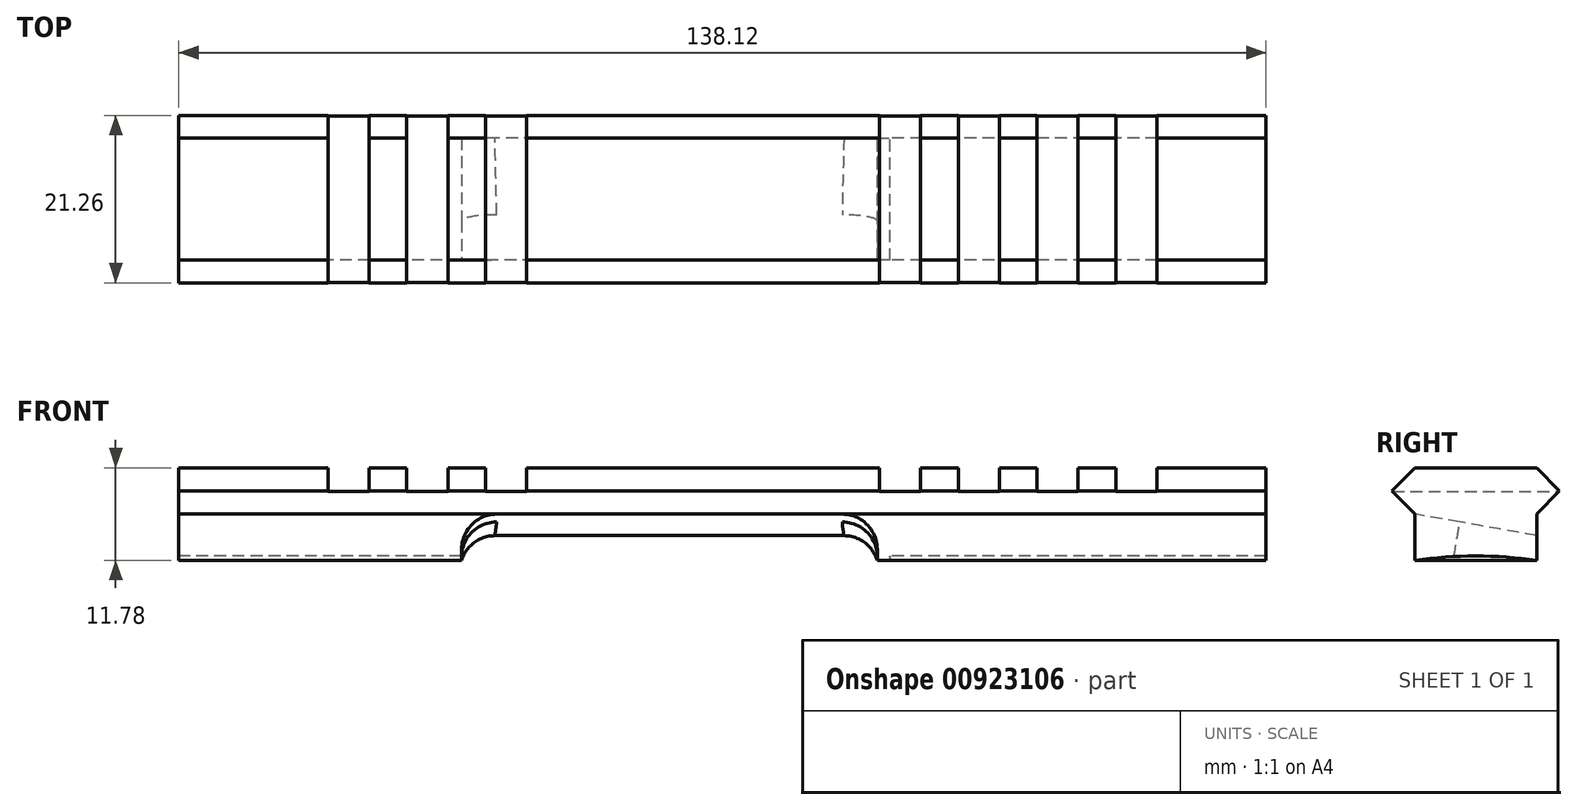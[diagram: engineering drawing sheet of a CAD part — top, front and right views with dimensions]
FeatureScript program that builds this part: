
annotation { "Feature Type Name" : "Feature", "Feature Type Description" : "" }
export const myFeature = defineFeature(function(context is Context, id is Id, definition is map)
    precondition{}
    {
        {
            var Q0;
            Q0=qCreatedBy(makeId("Right.planeOp"),FACE);
            var sketch = newSketch(context, id + "F0", { "sketchPlane" : qUnion([Q0])});
            skArc(sketch, "E0", {"start": v(15.26, -7.75) * mm, "mid": v(15.69, -3.88) * mm, "end": v(15.83, 0) * mm});
            skPoint(sketch, "E1.start.orphan", {"position": v(0, -7.82) * mm});
            skLineSegment(sketch, "E2.bottom", {"start": v(15.26, -7.75) * mm, "end": v(21.15, -7.75) * mm});
            skLineSegment(sketch, "E2.right", {"start": v(27.04, -7.75) * mm, "end": v(27.04, 0) * mm});
            skLineSegment(sketch, "E3", {"start": v(27.04, -7.75) * mm, "end": v(24.1, -10.63) * mm});
            skLineSegment(sketch, "E4", {"start": v(21.15, -7.75) * mm, "end": v(24.1, -10.63) * mm});
            skPoint(sketch, "E5.right.start.orphan", {"position": v(27.04, -7.75) * mm});
            skPoint(sketch, "E5.left.end.orphan", {"position": v(21.15, -10.63) * mm});
            skLineSegment(sketch, "E6", {"start": v(27.04, 0) * mm, "end": v(15.83, 0) * mm});
            skSolve(sketch);
        }
        {
            var Q0;
            Q0=makeQuery(id+"F0.imprint","IMPRINT",FACE,{"disambiguationData":[TD([[makeQuery(id+"F0.imprint","IMPRINT",EDGE,{"derivedFrom":sQuery(id+"F0.wireOp",EDGE,"E0")}),-1.0]])]});
            extrude(context, id + "F1", {"entities" : qUnion([Q0]), "depth" : 138.11 * mm, "offsetDistance" : 25.4 * mm, "symmetric" : true});
        }
        {
            var Q0;
            Q0=makeQuery(id+"F1.opExtrude","SWEPT_BODY",BODY,{"disambiguationData":[OSD([sQuery(id+"F0.wireOp",EDGE,"E0"),sQuery(id+"F0.wireOp",EDGE,"E2.bottom"),sQuery(id+"F0.wireOp",EDGE,"E2.right"),sQuery(id+"F0.wireOp",EDGE,"E3"),sQuery(id+"F0.wireOp",EDGE,"E4"),sQuery(id+"F0.wireOp",EDGE,"E6")])]});
            var Q1;
            Q1=qCreatedBy(makeId("Top.planeOp"),FACE);
            mirror(context, id + "F2", {"operationType" : NewBodyOperationType.ADD, "entities" : qUnion([Q0]), "mirrorPlane" : qUnion([Q1])});
        }
        {
            var Q0;
            Q0=qCreatedBy(makeId("Top.planeOp"),FACE);
            var sketch = newSketch(context, id + "F3", { "sketchPlane" : qUnion([Q0])});
            skLineSegment(sketch, "E7", {"start": v(0, 0) * mm, "end": v(78.36, 0) * mm});
            skSolve(sketch);
        }
        {
            var Q0;
            Q0=makeQuery(id+"F1.opExtrude","SWEPT_BODY",BODY,{"disambiguationData":[OSD([sQuery(id+"F0.wireOp",EDGE,"E0"),sQuery(id+"F0.wireOp",EDGE,"E2.bottom"),sQuery(id+"F0.wireOp",EDGE,"E2.right"),sQuery(id+"F0.wireOp",EDGE,"E3"),sQuery(id+"F0.wireOp",EDGE,"E4"),sQuery(id+"F0.wireOp",EDGE,"E6")])]});
            var Q1;
            Q1=sQuery(id+"F3.wireOp",VERTEX,"E7.start");
            var Q2;
            Q2=sQuery(id+"F3.wireOp",EDGE,"E7");
            transform(context, id + "F4", {"entities" : qUnion([Q0]), "transformType" : TransformType.ROTATION, "transformAxis" : qUnion([Q2]), "angle" : 90 * degree, "makeCopy" : false});
        }
        {
            var Q0;
            Q0=qCreatedBy(makeId("Front.planeOp"),FACE);
            var sketch = newSketch(context, id + "F5", { "sketchPlane" : qUnion([Q0])});
            skLineSegment(sketch, "E8.bottom", {"start": v(-50.1, 24.04) * mm, "end": v(-44.88, 24.04) * mm});
            skLineSegment(sketch, "E8.top", {"start": v(-50.1, 31.17) * mm, "end": v(-44.88, 31.17) * mm});
            skLineSegment(sketch, "E8.left", {"start": v(-50.1, 24.04) * mm, "end": v(-50.1, 31.17) * mm});
            skLineSegment(sketch, "E8.right", {"start": v(-44.88, 24.04) * mm, "end": v(-44.88, 31.17) * mm});
            skLineSegment(sketch, "E9.2.0.0", {"start": v(155.78, 24.04) * mm, "end": v(155.78, 31.17) * mm});
            skLineSegment(sketch, "E9.3.0.0", {"start": v(256.11, 24.04) * mm, "end": v(256.11, 31.17) * mm});
            skLineSegment(sketch, "E9.4.0.0", {"start": v(356.44, 24.04) * mm, "end": v(356.44, 31.17) * mm});
            skLineSegment(sketch, "E9.5.0.0", {"start": v(456.77, 24.04) * mm, "end": v(456.77, 31.17) * mm});
            skLineSegment(sketch, "E9.6.0.0", {"start": v(557.1, 24.04) * mm, "end": v(557.1, 31.17) * mm});
            skLineSegment(sketch, "E9.7.0.0", {"start": v(657.43, 24.04) * mm, "end": v(657.43, 31.17) * mm});
            skLineSegment(sketch, "E9.8.0.0", {"start": v(757.76, 24.04) * mm, "end": v(757.76, 31.17) * mm});
            skLineSegment(sketch, "E9.9.0.0", {"start": v(858.1, 24.04) * mm, "end": v(858.1, 31.17) * mm});
            skLineSegment(sketch, "E10.1.0.0", {"start": v(-40.1, 31.17) * mm, "end": v(-34.87, 31.17) * mm});
            skLineSegment(sketch, "E10.1.0.1", {"start": v(-40.1, 24.04) * mm, "end": v(-40.1, 31.17) * mm});
            skLineSegment(sketch, "E10.1.0.2", {"start": v(-40.1, 24.04) * mm, "end": v(-34.87, 24.04) * mm});
            skLineSegment(sketch, "E10.1.0.3", {"start": v(-34.87, 24.04) * mm, "end": v(-34.87, 31.17) * mm});
            skLineSegment(sketch, "E10.2.0.0", {"start": v(-30.1, 31.17) * mm, "end": v(-24.86, 31.17) * mm});
            skLineSegment(sketch, "E10.2.0.1", {"start": v(-30.1, 24.04) * mm, "end": v(-30.1, 31.17) * mm});
            skLineSegment(sketch, "E10.2.0.2", {"start": v(-30.1, 24.04) * mm, "end": v(-24.86, 24.04) * mm});
            skLineSegment(sketch, "E10.2.0.3", {"start": v(-24.86, 24.04) * mm, "end": v(-24.86, 31.17) * mm});
            skLineSegment(sketch, "E10.direction1", {"start": v(-50.1, 31.17) * mm, "end": v(-40.1, 31.17) * mm, "construction": true});
            skLineSegment(sketch, "E11.0.7.0", {"start": v(19.95, 31.17) * mm, "end": v(25.17, 31.17) * mm});
            skLineSegment(sketch, "E11.3.7.0", {"start": v(19.95, 24.04) * mm, "end": v(19.95, 31.17) * mm});
            skLineSegment(sketch, "E11.6.7.0", {"start": v(19.95, 24.04) * mm, "end": v(25.17, 24.04) * mm});
            skLineSegment(sketch, "E11.9.7.0", {"start": v(25.17, 24.04) * mm, "end": v(25.17, 31.17) * mm});
            skLineSegment(sketch, "E11.0.8.0", {"start": v(29.95, 31.17) * mm, "end": v(35.18, 31.17) * mm});
            skLineSegment(sketch, "E11.3.8.0", {"start": v(29.95, 24.04) * mm, "end": v(29.95, 31.17) * mm});
            skLineSegment(sketch, "E11.6.8.0", {"start": v(29.95, 24.04) * mm, "end": v(35.18, 24.04) * mm});
            skLineSegment(sketch, "E11.9.8.0", {"start": v(35.18, 24.04) * mm, "end": v(35.18, 31.17) * mm});
            skLineSegment(sketch, "E11.0.9.0", {"start": v(39.96, 31.17) * mm, "end": v(45.19, 31.17) * mm});
            skLineSegment(sketch, "E11.3.9.0", {"start": v(39.96, 24.04) * mm, "end": v(39.96, 31.17) * mm});
            skLineSegment(sketch, "E11.6.9.0", {"start": v(39.96, 24.04) * mm, "end": v(45.19, 24.04) * mm});
            skLineSegment(sketch, "E11.9.9.0", {"start": v(45.19, 24.04) * mm, "end": v(45.19, 31.17) * mm});
            skLineSegment(sketch, "E12.0.10.0", {"start": v(49.97, 31.17) * mm, "end": v(55.2, 31.17) * mm});
            skLineSegment(sketch, "E12.3.10.0", {"start": v(49.97, 24.04) * mm, "end": v(49.97, 31.17) * mm});
            skLineSegment(sketch, "E12.6.10.0", {"start": v(49.97, 24.04) * mm, "end": v(55.2, 24.04) * mm});
            skLineSegment(sketch, "E12.9.10.0", {"start": v(55.2, 24.04) * mm, "end": v(55.2, 31.17) * mm});
            skSolve(sketch);
        }
        {
            var Q0;
            Q0=makeQuery(id+"F5.imprint","IMPRINT",FACE,{"disambiguationData":[TD([[makeQuery(id+"F5.imprint","IMPRINT",EDGE,{"derivedFrom":sQuery(id+"F5.wireOp",EDGE,"E8.bottom")}),1.0]])]});
            var Q1;
            Q1=makeQuery(id+"F5.imprint","IMPRINT",FACE,{"disambiguationData":[TD([[makeQuery(id+"F5.imprint","IMPRINT",EDGE,{"derivedFrom":sQuery(id+"F5.wireOp",EDGE,"E10.1.0.0")}),-1.0]])]});
            var Q2;
            Q2=makeQuery(id+"F5.imprint","IMPRINT",FACE,{"disambiguationData":[TD([[makeQuery(id+"F5.imprint","IMPRINT",EDGE,{"derivedFrom":sQuery(id+"F5.wireOp",EDGE,"E10.2.0.0")}),-1.0]])]});
            var Q3;
            Q3=makeQuery(id+"F5.imprint","IMPRINT",FACE,{"disambiguationData":[TD([[makeQuery(id+"F5.imprint","IMPRINT",EDGE,{"derivedFrom":sQuery(id+"F5.wireOp",EDGE,"E11.0.3.0")}),-1.0]])]});
            var Q4;
            Q4=makeQuery(id+"F5.imprint","IMPRINT",FACE,{"disambiguationData":[TD([[makeQuery(id+"F5.imprint","IMPRINT",EDGE,{"derivedFrom":sQuery(id+"F5.wireOp",EDGE,"E11.0.4.0")}),-1.0]])]});
            var Q5;
            Q5=makeQuery(id+"F5.imprint","IMPRINT",FACE,{"disambiguationData":[TD([[makeQuery(id+"F5.imprint","IMPRINT",EDGE,{"derivedFrom":sQuery(id+"F5.wireOp",EDGE,"E11.0.5.0")}),-1.0]])]});
            var Q6;
            Q6=makeQuery(id+"F5.imprint","IMPRINT",FACE,{"disambiguationData":[TD([[makeQuery(id+"F5.imprint","IMPRINT",EDGE,{"derivedFrom":sQuery(id+"F5.wireOp",EDGE,"E11.0.6.0")}),-1.0]])]});
            var Q7;
            Q7=makeQuery(id+"F5.imprint","IMPRINT",FACE,{"disambiguationData":[TD([[makeQuery(id+"F5.imprint","IMPRINT",EDGE,{"derivedFrom":sQuery(id+"F5.wireOp",EDGE,"E11.0.7.0")}),-1.0]])]});
            var Q8;
            Q8=makeQuery(id+"F5.imprint","IMPRINT",FACE,{"disambiguationData":[TD([[makeQuery(id+"F5.imprint","IMPRINT",EDGE,{"derivedFrom":sQuery(id+"F5.wireOp",EDGE,"E11.0.8.0")}),-1.0]])]});
            var Q9;
            Q9=makeQuery(id+"F5.imprint","IMPRINT",FACE,{"disambiguationData":[TD([[makeQuery(id+"F5.imprint","IMPRINT",EDGE,{"derivedFrom":sQuery(id+"F5.wireOp",EDGE,"E11.0.9.0")}),-1.0]])]});
            var Q10;
            Q10=makeQuery(id+"F5.imprint","IMPRINT",FACE,{"disambiguationData":[TD([[makeQuery(id+"F5.imprint","IMPRINT",EDGE,{"derivedFrom":sQuery(id+"F5.wireOp",EDGE,"E12.0.10.0")}),-1.0]])]});
            extrude(context, id + "F6", {"entities" : qUnion([Q0, Q1, Q2, Q3, Q4, Q5, Q6, Q7, Q8, Q9, Q10]), "operationType" : NewBodyOperationType.REMOVE, "depth" : 25.4 * mm, "offsetDistance" : 25.4 * mm, "symmetric" : true});
        }
        {
            var Q0;
            Q0=makeQuery(id+"F2.opPattern","COPY",FACE,{"derivedFrom":makeQuery(id+"F1.opExtrude","SWEPT_FACE",FACE,{"disambiguationData":[OSD([sQuery(id+"F0.wireOp",EDGE,"E2.bottom")])]}),"instanceName":"1"});
            var sketch = newSketch(context, id + "F7", { "sketchPlane" : qUnion([Q0])});
            skLineSegment(sketch, "E13.bottom", {"start": v(-33.14, -3.06) * mm, "end": v(19.67, -3.06) * mm});
            skLineSegment(sketch, "E13.top", {"start": v(-33.14, 21.15) * mm, "end": v(19.67, 21.15) * mm});
            skLineSegment(sketch, "E13.left", {"start": v(-33.14, -3.06) * mm, "end": v(-33.14, 21.15) * mm});
            skLineSegment(sketch, "E13.right", {"start": v(19.67, -3.06) * mm, "end": v(19.67, 21.15) * mm});
            skSolve(sketch);
        }
        {
            var Q0;
            {var subQ0=sQuery(id+"F7.wireOp",EDGE,"E13.bottom");Q0=makeQuery(id+"F7.imprint","IMPRINT",FACE,{"disambiguationData":[TD([[makeQuery(id+"F7.imprint","IMPRINT",EDGE,{"derivedFrom":subQ0}),1.0]])]});}
            var sketch = newSketch(context, id + "F8", { "sketchPlane" : qUnion([Q0])});
            skLineSegment(sketch, "E14.0", {"start": v(-33.14, 21.15) * mm, "end": v(19.67, 21.15) * mm});
            skSolve(sketch);
        }
        {
            var Q0;
            {var subQ0=sQuery(id+"F7.wireOp",EDGE,"E13.bottom");Q0=makeQuery(id+"F7.imprint","IMPRINT",FACE,{"disambiguationData":[TD([[makeQuery(id+"F7.imprint","IMPRINT",EDGE,{"derivedFrom":subQ0}),1.0]])]});}
            var Q1;
            {var subQ0=sQuery(id+"F7.wireOp",EDGE,"E13.top");Q1=makeQuery(id+"F7.imprint","IMPRINT",FACE,{"disambiguationData":[TD([[makeQuery(id+"F7.imprint","IMPRINT",EDGE,{"derivedFrom":subQ0}),1.0]])]});}
            extrude(context, id + "F9", {"entities" : qUnion([Q0, Q1]), "oppositeDirection" : true, "depth" : 25.4 * mm, "offsetDistance" : 25.4 * mm});
        }
        {
            var Q0;
            Q0=makeQuery(id+"F9.opExtrude","SWEPT_BODY",BODY,{"disambiguationData":[OSD([sQuery(id+"F7.wireOp",EDGE,"E13.bottom"),sQuery(id+"F7.wireOp",EDGE,"E13.top"),sQuery(id+"F7.wireOp",EDGE,"E13.left"),sQuery(id+"F7.wireOp",EDGE,"E13.right")])]});
            var Q1;
            Q1=sQuery(id+"F8.wireOp",EDGE,"E14.0");
            transform(context, id + "F10", {"entities" : qUnion([Q0]), "transformType" : TransformType.ROTATION, "transformAxis" : qUnion([Q1]), "angle" : 350 * degree, "makeCopy" : false});
        }
        {
            var Q0;
            Q0=makeQuery(id+"F9.opExtrude","SWEPT_BODY",BODY,{"disambiguationData":[OSD([sQuery(id+"F7.wireOp",EDGE,"E13.bottom"),sQuery(id+"F7.wireOp",EDGE,"E13.top"),sQuery(id+"F7.wireOp",EDGE,"E13.left"),sQuery(id+"F7.wireOp",EDGE,"E13.right")])]});
            var Q1;
            Q1=makeQuery(id+"F1.opExtrude","SWEPT_BODY",BODY,{"disambiguationData":[OSD([sQuery(id+"F0.wireOp",EDGE,"E0"),sQuery(id+"F0.wireOp",EDGE,"E2.bottom"),sQuery(id+"F0.wireOp",EDGE,"E2.right"),sQuery(id+"F0.wireOp",EDGE,"E3"),sQuery(id+"F0.wireOp",EDGE,"E4"),sQuery(id+"F0.wireOp",EDGE,"E6")])]});
            booleanBodies(context, id + "F11", {"operationType" : BooleanOperationType.SUBTRACTION, "tools" : qUnion([Q0]), "targets" : qUnion([Q1])});
        }
        {
            var Q0;
            Q0=makeQuery(id+"F11.opBoolean","COPY",EDGE,{"derivedFrom":makeQuery(id+"F9.opExtrude","SWEPT_EDGE",EDGE,{"disambiguationData":[OSD([sQuery(id+"F0.wireOp",EDGE,"E2.bottom"),sQuery(id+"F0.wireOp",EDGE,"E4"),sQuery(id+"F7.wireOp",EDGE,"E13.top"),sQuery(id+"F7.wireOp",EDGE,"E13.left")])]})});
            var Q1;
            Q1=makeQuery(id+"F11.opBoolean","COPY",EDGE,{"derivedFrom":makeQuery(id+"F9.opExtrude","SWEPT_EDGE",EDGE,{"disambiguationData":[OSD([sQuery(id+"F0.wireOp",EDGE,"E2.bottom"),sQuery(id+"F0.wireOp",EDGE,"E4"),sQuery(id+"F7.wireOp",EDGE,"E13.top"),sQuery(id+"F7.wireOp",EDGE,"E13.right")])]})});
            fillet(context, id + "F12", {"entities" : qUnion([Q0, Q1]), "radius" : 4.44 * mm, "tangentPropagation" : true, "allowEdgeOverflow" : false});
        }
        {
            var Q0;
            Q0=makeQuery(id+"F11.opBoolean","COPY",FACE,{"derivedFrom":makeQuery(id+"F9.opExtrude","SWEPT_FACE",FACE,{"disambiguationData":[OSD([sQuery(id+"F7.wireOp",EDGE,"E13.right")])]})});
            var sketch = newSketch(context, id + "F13", { "sketchPlane" : qUnion([Q0])});
            skLineSegment(sketch, "E15", {"start": v(7.75, 15.26) * mm, "end": v(-7.74, 15.26) * mm});
            skLineSegment(sketch, "E16", {"start": v(-7.74, 15.26) * mm, "end": v(-7.74, 16.58) * mm});
            skLineSegment(sketch, "E17", {"start": v(-7.74, 16.58) * mm, "end": v(7.75, 16.64) * mm});
            skLineSegment(sketch, "E18", {"start": v(7.75, 16.64) * mm, "end": v(7.75, 15.26) * mm});
            skSolve(sketch);
        }
        {
            var Q0;
            Q0 = qSketchRegion(id + "F13", true);
            extrude(context, id + "F14", {"entities" : qUnion([Q0]), "operationType" : NewBodyOperationType.ADD, "oppositeDirection" : true, "depth" : 1.59 * mm, "offsetDistance" : 25.4 * mm});
        }
    });
